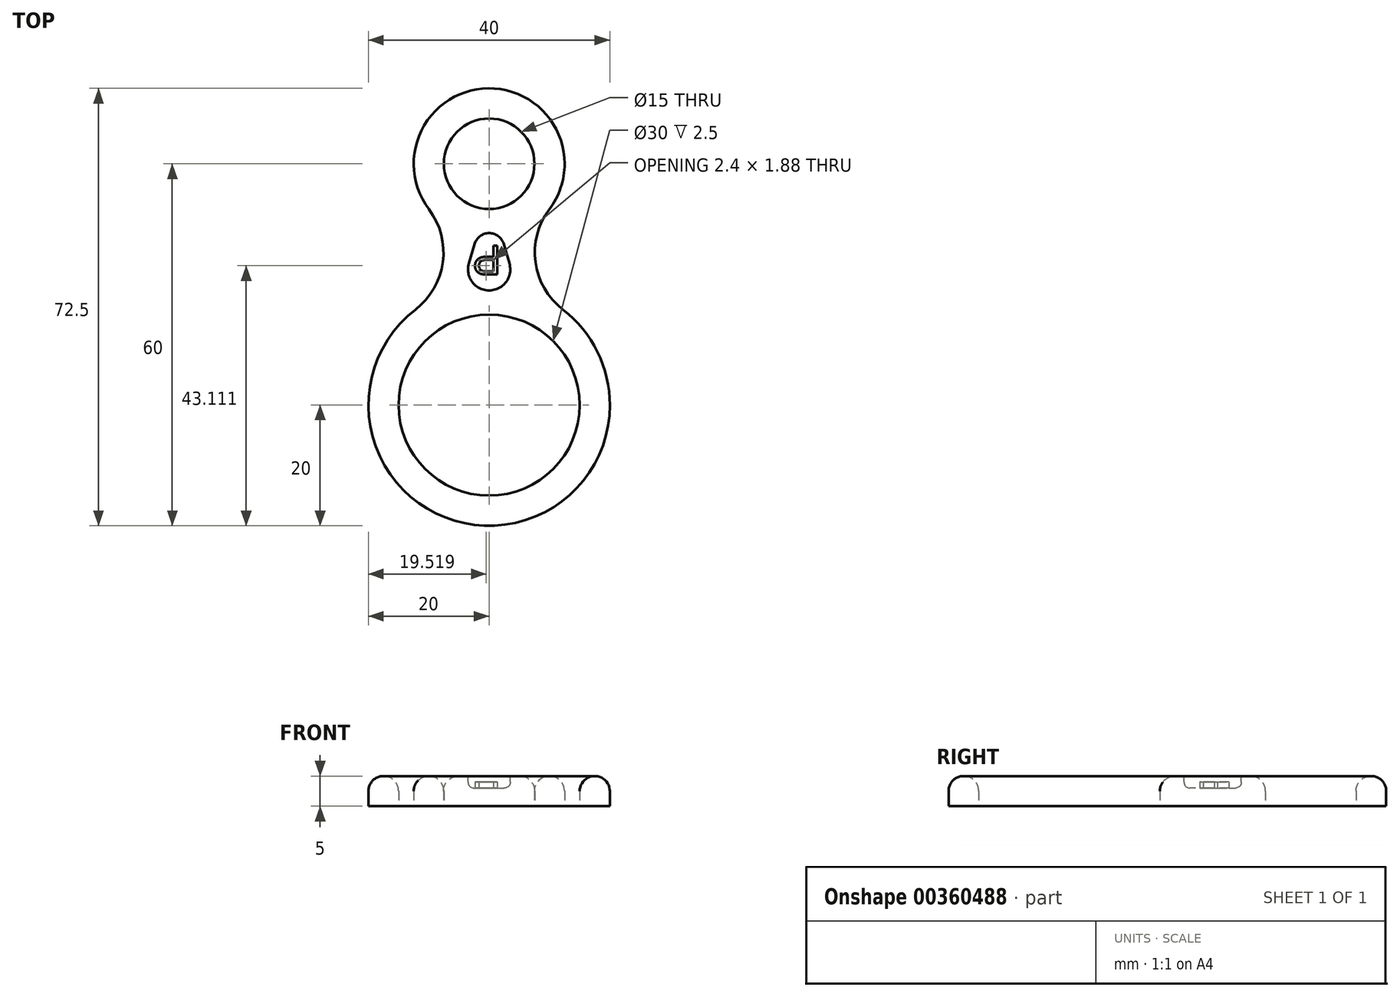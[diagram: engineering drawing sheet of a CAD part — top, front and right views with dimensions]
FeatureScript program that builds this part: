
annotation { "Feature Type Name" : "Feature", "Feature Type Description" : "" }
export const myFeature = defineFeature(function(context is Context, id is Id, definition is map)
    precondition{}
    {
        {
            var Q0;
            Q0=qCreatedBy(makeId("Top.planeOp"),FACE);
            var sketch = newSketch(context, id + "F0", { "sketchPlane" : qUnion([Q0])});
            skCircle(sketch, "E0", {"center": v(0, 40) * mm, "radius": 7.5 * mm});
            skCircle(sketch, "E1", {"center": v(0, 0) * mm, "radius": 15 * mm});
            skArc(sketch, "E2.0", {"start": v(-12.21, 15.84) * mm, "mid": v(0, -20) * mm, "end": v(12.21, 15.84) * mm});
            skLineSegment(sketch, "E3", {"start": v(-7.57, 25.28) * mm, "end": v(39.99, 25.28) * mm, "construction": true});
            skArc(sketch, "E4", {"start": v(-12.21, 15.84) * mm, "mid": v(-7.68, 23.7) * mm, "end": v(-9.98, 32.47) * mm});
            skArc(sketch, "E5.MirrorCS", {"start": v(12.21, 15.84) * mm, "mid": v(7.68, 23.7) * mm, "end": v(9.98, 32.47) * mm});
            skArc(sketch, "E6.trimOffspring", {"start": v(9.98, 32.47) * mm, "mid": v(0, 52.5) * mm, "end": v(-9.98, 32.47) * mm});
            skSolve(sketch);
        }
        {
            var Q0;
            Q0 = qSketchRegion(id + "F0", true);
            extrude(context, id + "F1", {"entities" : qUnion([Q0]), "depth" : 5 * mm});
        }
        {
            var Q0;
            Q0=makeQuery(id+"F1.opExtrude","CAP_FACE",FACE,{"disambiguationData":[OSD([sQuery(id+"F0.wireOp",EDGE,"E0"),sQuery(id+"F0.wireOp",EDGE,"E1"),sQuery(id+"F0.wireOp",EDGE,"E2.0"),sQuery(id+"F0.wireOp",EDGE,"E4"),sQuery(id+"F0.wireOp",EDGE,"E5.MirrorCS"),sQuery(id+"F0.wireOp",EDGE,"E6.trimOffspring")])],"isStart":false});
            fillet(context, id + "F2", {"entities" : qUnion([Q0]), "radius" : 2.5 * mm, "tangentPropagation" : true, "allowEdgeOverflow" : false});
        }
        {
            var Q0;
            Q0=makeQuery(id+"F1.opExtrude","CAP_FACE",FACE,{"disambiguationData":[OSD([sQuery(id+"F0.wireOp",EDGE,"E0"),sQuery(id+"F0.wireOp",EDGE,"E1"),sQuery(id+"F0.wireOp",EDGE,"E2.0"),sQuery(id+"F0.wireOp",EDGE,"E4"),sQuery(id+"F0.wireOp",EDGE,"E5.MirrorCS"),sQuery(id+"F0.wireOp",EDGE,"E6.trimOffspring")])],"isStart":false});
            var sketch = newSketch(context, id + "F3", { "sketchPlane" : qUnion([Q0])});
            skArc(sketch, "E7", {"start": v(2.4, 26.71) * mm, "mid": v(0, 28.5) * mm, "end": v(-2.4, 26.71) * mm});
            skArc(sketch, "E8", {"start": v(-3.35, 23.5) * mm, "mid": v(0, 19) * mm, "end": v(3.35, 23.5) * mm});
            skLineSegment(sketch, "E9", {"start": v(-2.4, 26.71) * mm, "end": v(-3.35, 23.5) * mm});
            skLineSegment(sketch, "E10.MirrorCS", {"start": v(2.4, 26.71) * mm, "end": v(3.35, 23.5) * mm});
            skSolve(sketch);
        }
        {
            var Q0;
            Q0 = qSketchRegion(id + "F3", true);
            extrude(context, id + "F4", {"entities" : qUnion([Q0]), "operationType" : NewBodyOperationType.REMOVE, "oppositeDirection" : true, "depth" : 2 * mm});
        }
        {
            var Q0;
            Q0=makeQuery(id+"F4.boolean.opBoolean","COPY",EDGE,{"derivedFrom":makeQuery(id+"F4.opExtrude","CAP_EDGE",EDGE,{"disambiguationData":[OSD([sQuery(id+"F3.wireOp",EDGE,"E7")])],"isStart":true})});
            var Q1;
            Q1=makeQuery(id+"F4.boolean.opBoolean","COPY",EDGE,{"derivedFrom":makeQuery(id+"F4.opExtrude","CAP_EDGE",EDGE,{"disambiguationData":[OSD([sQuery(id+"F3.wireOp",EDGE,"E7")])],"isStart":false})});
            fillet(context, id + "F5", {"entities" : qUnion([Q0, Q1]), "radius" : 1 * mm, "tangentPropagation" : true, "allowEdgeOverflow" : false});
        }
        {
            var Q0;
            Q0=makeQuery(id+"F4.boolean.opBoolean","COPY",FACE,{"derivedFrom":makeQuery(id+"F4.opExtrude","CAP_FACE",FACE,{"disambiguationData":[OSD([sQuery(id+"F3.wireOp",EDGE,"E7"),sQuery(id+"F3.wireOp",EDGE,"E8"),sQuery(id+"F3.wireOp",EDGE,"E9"),sQuery(id+"F3.wireOp",EDGE,"E10.MirrorCS")])],"isStart":false})});
            var sketch = newSketch(context, id + "F6", { "sketchPlane" : qUnion([Q0])});
            skText(sketch, "E11", { "text": "P", "fontName": "Arimo-Regular.ttf"});
            const initialGuessF6  = {"E11": [-0.0033, 0.02143, 1, 0, 0.005]};
            skSetInitialGuess(sketch, initialGuessF6);
            skSolve(sketch);
        }
        {
            var Q0;
            Q0 = qSketchRegion(id + "F6", true);
            extrude(context, id + "F7", {"entities" : qUnion([Q0]), "depth" : 1 * mm});
        }
        {
            var Q0;
            Q0=makeQuery(id+"F7.opExtrude","CAP_FACE",FACE,{"disambiguationData":[OSD([sQuery(id+"F6.wireOp",EDGE,"E11.sketch_text.stroke-0"),sQuery(id+"F6.wireOp",EDGE,"E11.sketch_text.stroke-1"),sQuery(id+"F6.wireOp",EDGE,"E11.sketch_text.stroke-2"),sQuery(id+"F6.wireOp",EDGE,"E11.sketch_text.stroke-3"),sQuery(id+"F6.wireOp",EDGE,"E11.sketch_text.stroke-4"),sQuery(id+"F6.wireOp",EDGE,"E11.sketch_text.stroke-5"),sQuery(id+"F6.wireOp",EDGE,"E11.sketch_text.stroke-6"),sQuery(id+"F6.wireOp",EDGE,"E11.sketch_text.stroke-7"),sQuery(id+"F6.wireOp",EDGE,"E11.sketch_text.stroke-8"),sQuery(id+"F6.wireOp",EDGE,"E11.sketch_text.stroke-9"),sQuery(id+"F6.wireOp",EDGE,"E11.sketch_text.stroke-10"),sQuery(id+"F6.wireOp",EDGE,"E11.sketch_text.stroke-11"),sQuery(id+"F6.wireOp",EDGE,"E11.sketch_text.stroke-12"),sQuery(id+"F6.wireOp",EDGE,"E11.sketch_text.stroke-13")])],"isStart":false});
            var sketch = newSketch(context, id + "F8", { "sketchPlane" : qUnion([Q0])});
            skCircle(sketch, "E12", {"center": v(-2.73, 21.43) * mm, "radius": 8.73 * mm});
            skSolve(sketch);
        }
        {
            var Q0;
            Q0=makeQuery(id+"F7.opExtrude","SWEPT_BODY",BODY,{"disambiguationData":[OSD([sQuery(id+"F6.wireOp",EDGE,"E11.sketch_text.stroke-0"),sQuery(id+"F6.wireOp",EDGE,"E11.sketch_text.stroke-1"),sQuery(id+"F6.wireOp",EDGE,"E11.sketch_text.stroke-2"),sQuery(id+"F6.wireOp",EDGE,"E11.sketch_text.stroke-3"),sQuery(id+"F6.wireOp",EDGE,"E11.sketch_text.stroke-4"),sQuery(id+"F6.wireOp",EDGE,"E11.sketch_text.stroke-5"),sQuery(id+"F6.wireOp",EDGE,"E11.sketch_text.stroke-6"),sQuery(id+"F6.wireOp",EDGE,"E11.sketch_text.stroke-7"),sQuery(id+"F6.wireOp",EDGE,"E11.sketch_text.stroke-8"),sQuery(id+"F6.wireOp",EDGE,"E11.sketch_text.stroke-9"),sQuery(id+"F6.wireOp",EDGE,"E11.sketch_text.stroke-10"),sQuery(id+"F6.wireOp",EDGE,"E11.sketch_text.stroke-11"),sQuery(id+"F6.wireOp",EDGE,"E11.sketch_text.stroke-12"),sQuery(id+"F6.wireOp",EDGE,"E11.sketch_text.stroke-13")])]});
            var Q1;
            Q1=sQuery(id+"F8.wireOp",EDGE,"E12");
            transform(context, id + "F9", {"entities" : qUnion([Q0]), "transformType" : TransformType.ROTATION, "transformAxis" : qUnion([Q1]), "angle" : 180 * degree, "makeCopy" : false});
        }
        {
            var Q0;
            Q0=makeQuery(id+"F7.opExtrude","SWEPT_BODY",BODY,{"disambiguationData":[OSD([sQuery(id+"F6.wireOp",EDGE,"E11.sketch_text.stroke-0"),sQuery(id+"F6.wireOp",EDGE,"E11.sketch_text.stroke-1"),sQuery(id+"F6.wireOp",EDGE,"E11.sketch_text.stroke-2"),sQuery(id+"F6.wireOp",EDGE,"E11.sketch_text.stroke-3"),sQuery(id+"F6.wireOp",EDGE,"E11.sketch_text.stroke-4"),sQuery(id+"F6.wireOp",EDGE,"E11.sketch_text.stroke-5"),sQuery(id+"F6.wireOp",EDGE,"E11.sketch_text.stroke-6"),sQuery(id+"F6.wireOp",EDGE,"E11.sketch_text.stroke-7"),sQuery(id+"F6.wireOp",EDGE,"E11.sketch_text.stroke-8"),sQuery(id+"F6.wireOp",EDGE,"E11.sketch_text.stroke-9"),sQuery(id+"F6.wireOp",EDGE,"E11.sketch_text.stroke-10"),sQuery(id+"F6.wireOp",EDGE,"E11.sketch_text.stroke-11"),sQuery(id+"F6.wireOp",EDGE,"E11.sketch_text.stroke-12"),sQuery(id+"F6.wireOp",EDGE,"E11.sketch_text.stroke-13")])]});
            transform(context, id + "F10", {"entities" : qUnion([Q0]), "transformType" : TransformType.TRANSLATION_3D, "dx" : 4.1 * mm, "dy" : 5 * mm, "dz" : 0 * mm, "makeCopy" : false});
        }
    });
